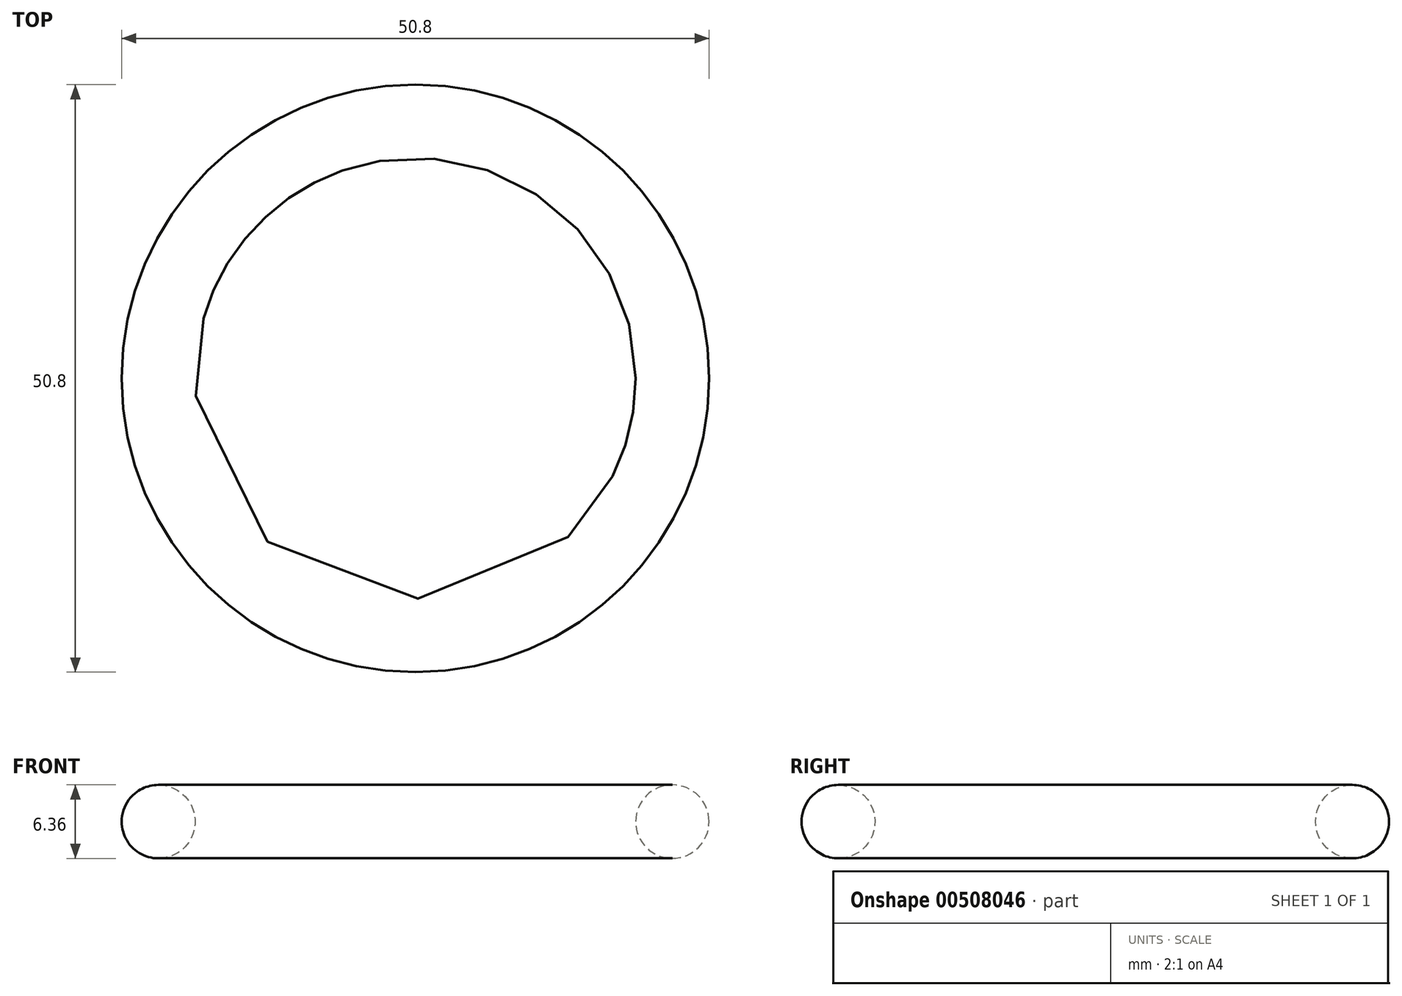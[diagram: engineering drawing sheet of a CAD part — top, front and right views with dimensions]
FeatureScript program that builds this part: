
annotation { "Feature Type Name" : "Feature", "Feature Type Description" : "" }
export const myFeature = defineFeature(function(context is Context, id is Id, definition is map)
    precondition{}
    {
        {
            var Q0;
            Q0=qCreatedBy(makeId("Front.planeOp"),FACE);
            var sketch = newSketch(context, id + "F0", { "sketchPlane" : qUnion([Q0])});
            skCircle(sketch, "E0", {"center": v(-22.23, 0) * mm, "radius": 3.18 * mm});
            skLineSegment(sketch, "E1", {"start": v(0, 9.1) * mm, "end": v(0, -8.58) * mm, "construction": true});
            skSolve(sketch);
        }
        {
            var Q0;
            Q0 = qSketchRegion(id + "F0", true);
            var Q1;
            Q1=sQuery(id+"F0.wireOp",EDGE,"E1");
            revolve(context, id + "F1", {"entities" : qUnion([Q0]), "axis" : qUnion([Q1]), "revolveType" : RevolveType.FULL});
        }
    });
